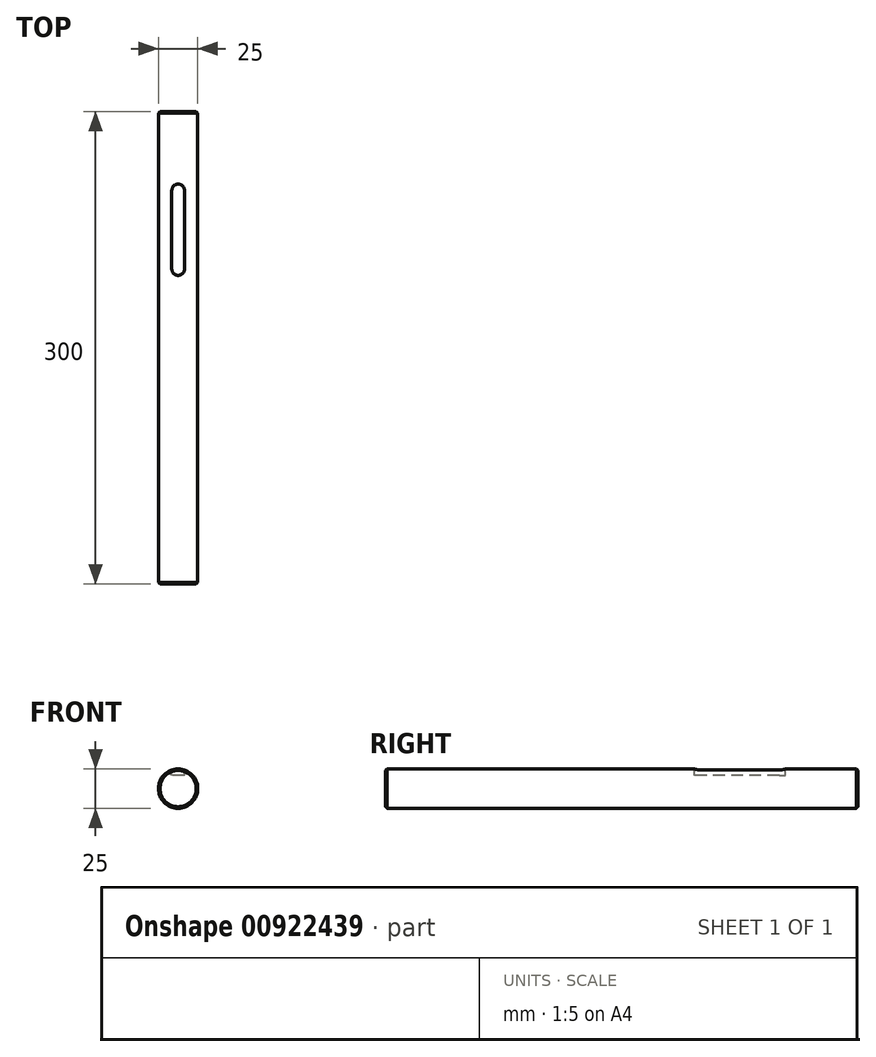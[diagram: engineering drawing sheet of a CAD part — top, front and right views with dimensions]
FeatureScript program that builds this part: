
annotation { "Feature Type Name" : "Feature", "Feature Type Description" : "" }
export const myFeature = defineFeature(function(context is Context, id is Id, definition is map)
    precondition{}
    {
        {
            var Q0;
            Q0=qCreatedBy(makeId("Front.planeOp"),FACE);
            var sketch = newSketch(context, id + "F0", { "sketchPlane" : qUnion([Q0])});
            skCircle(sketch, "E0", {"center": v(0, 0) * mm, "radius": 12.5 * mm});
            skSolve(sketch);
        }
        {
            var Q0;
            Q0=makeQuery(id+"F0.imprint","IMPRINT",FACE,{"disambiguationData":[TD([[makeQuery(id+"F0.imprint","IMPRINT",EDGE,{"derivedFrom":sQuery(id+"F0.wireOp",EDGE,"E0")}),1.0]])]});
            extrude(context, id + "F1", {"entities" : qUnion([Q0]), "endBound" : BoundingType.SYMMETRIC, "depth" : 300 * mm, "offsetDistance" : 25 * mm});
        }
        {
            var Q0;
            Q0=qCreatedBy(makeId("Top.planeOp"),FACE);
            cPlane(context, id + "F2", {"entities" : qUnion([Q0]), "cplaneType" : CPlaneType.OFFSET, "offset" : 12.5 * mm, "width" : 150 * mm, "height" : 150 * mm});
        }
        {
            var Q0;
            Q0=qCreatedBy(id+"F2.planeOp",FACE);
            var sketch = newSketch(context, id + "F3", { "sketchPlane" : qUnion([Q0])});
            skArc(sketch, "E1", {"start": v(4, 100) * mm, "mid": v(0, 104) * mm, "end": v(-4, 100) * mm});
            skArc(sketch, "E2", {"start": v(-4, 50) * mm, "mid": v(0, 46) * mm, "end": v(4, 50) * mm});
            skLineSegment(sketch, "E3", {"start": v(-4, 100) * mm, "end": v(-4, 50) * mm});
            skLineSegment(sketch, "E4", {"start": v(4, 100) * mm, "end": v(4, 50) * mm});
            skSolve(sketch);
        }
        {
            var Q0;
            Q0=makeQuery(id+"F3.imprint","IMPRINT",FACE,{"disambiguationData":[TD([[makeQuery(id+"F3.imprint","IMPRINT",EDGE,{"derivedFrom":sQuery(id+"F3.wireOp",EDGE,"E1")}),1.0]])]});
            extrude(context, id + "F4", {"entities" : qUnion([Q0]), "operationType" : NewBodyOperationType.REMOVE, "oppositeDirection" : true, "depth" : 4 * mm, "offsetDistance" : 25 * mm});
        }
        {
            var Q0;
            Q0=makeQuery(id+"F1.opExtrude","CAP_EDGE",EDGE,{"disambiguationData":[OSD([sQuery(id+"F0.wireOp",EDGE,"E0")])],"isStart":true});
            var Q1;
            Q1=makeQuery(id+"F1.opExtrude","CAP_EDGE",EDGE,{"disambiguationData":[OSD([sQuery(id+"F0.wireOp",EDGE,"E0")])],"isStart":false});
            chamfer(context, id + "F5", {"entities" : qUnion([Q0, Q1]), "width" : 1 * mm, "tangentPropagation" : true});
        }
    });
